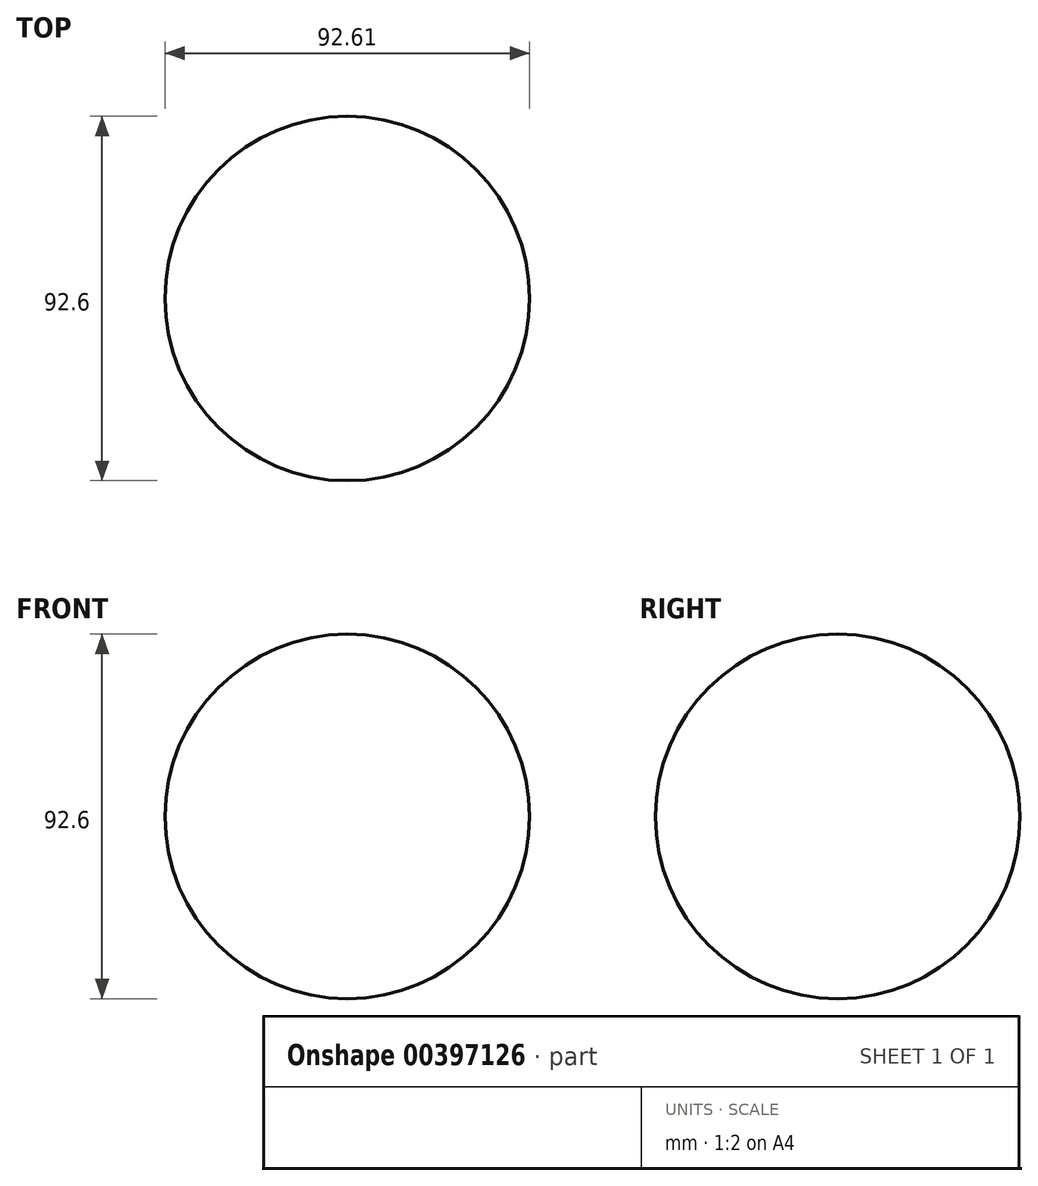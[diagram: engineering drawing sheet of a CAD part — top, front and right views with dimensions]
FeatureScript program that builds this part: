
annotation { "Feature Type Name" : "Feature", "Feature Type Description" : "" }
export const myFeature = defineFeature(function(context is Context, id is Id, definition is map)
    precondition{}
    {
        {
            var Q0;
            Q0=qCreatedBy(makeId("Top.planeOp"),FACE);
            var sketch = newSketch(context, id + "F0", { "sketchPlane" : qUnion([Q0])});
            skArc(sketch, "E0", {"start": v(49.18, 0) * mm, "mid": v(2.88, 46.3) * mm, "end": v(-43.43, 0) * mm});
            skLineSegment(sketch, "E1", {"start": v(-43.43, 0) * mm, "end": v(49.18, 0) * mm});
            skSolve(sketch);
        }
        {
            var Q0;
            Q0 = qSketchRegion(id + "F0", true);
            var Q1;
            Q1=sQuery(id+"F0.wireOp",EDGE,"E1");
            revolve(context, id + "F1", {"entities" : qUnion([Q0]), "axis" : qUnion([Q1]), "revolveType" : RevolveType.FULL});
        }
    });
